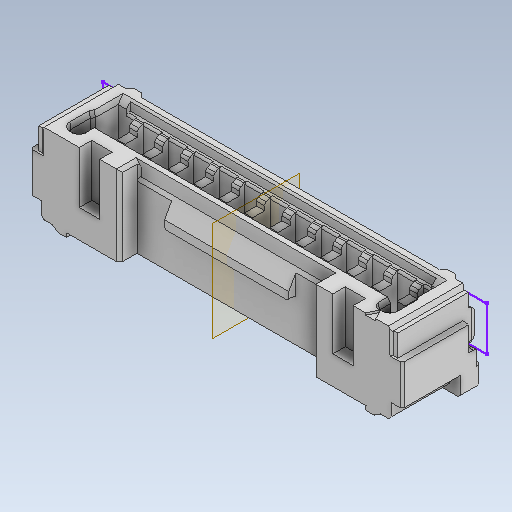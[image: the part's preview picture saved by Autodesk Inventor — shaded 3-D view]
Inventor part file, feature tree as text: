
AUTODESK INVENTOR PART (.ipt)
format: ipt  version: 2021 (Build 250183000, 183)  size: 535,040 bytes
history: native  units: mm
features: other x1, imported_body x1, plane x1, sketch x1
ambient origin geometry x8: Origin, YZ Plane, XZ Plane, XY Plane, X Axis, Y Axis, Z Axis, Center Point
bodies: Solid1 (feature_tree)
feature tree (4):
  other  "Repaired Geometry1"
  imported_body  "Base1"
  plane  "Work Plane1"
  sketch  "3D Sketch1"
